# Revit family: BIMLIB_КассетныйФильтр_FBCr _SHUFT
name_source: partatom
category: Арматура воздуховодов
revit_build: Autodesk Revit 2017 (Build: 20170118_1100(x64)
units: mm (PartAtom-declared; Revit-internal decimal feet)

## family parameters
Всегда вертикально = Да
На основе рабочей плоскости = Нет
Общий = Нет
При загрузке вырезать с полостями = Нет
Размер круглого соединителя = Использовать диаметр
Тип детали = Вставляется

## types (1)
- BIMLIB_КассетныйФильтр_FBCr _SHUFT
    ADSK_URL документации изделия = http://www.shuft.ru
    ADSK_URL страницы изделия = http://www.shuft.ru
    ADSK_Версия Revit = 2017
    ADSK_Версия семейства = v.1
    ADSK_Единица измерения = шт.
    ADSK_Завод-изготовитель = ООО «Завод ВКО» марка SHUFT
    ADSK_Материал = BIMLIB_Сталь_SHUFT
    BL_BIM library = https://bimlib.pro
    URL = http://www.shuft.ru
    Изготовитель = ООО «Завод ВКО» марка SHUFT
    Описание = Воздушные фильтры cерии FBCr предназначены для очистки от пыли наружного и рециркуляционного воздуха в системах приточной и вытяжной вентиляции.

Фильтруемый воздух не должен содержать агрессивных газов и паров. Корпус фильтра сделан из оцинкованной стали. В качестве фильтрующих вставок использован синтетический материал с классом очистки EU3. Корпус фильтра снабжен круглыми патрубками с резиновыми уплотнителями для подсоединения к другим элементам системы.

Фильтры FBCr можно устанавливать вертикально или горизонтально.
    Таблица = FBCr
